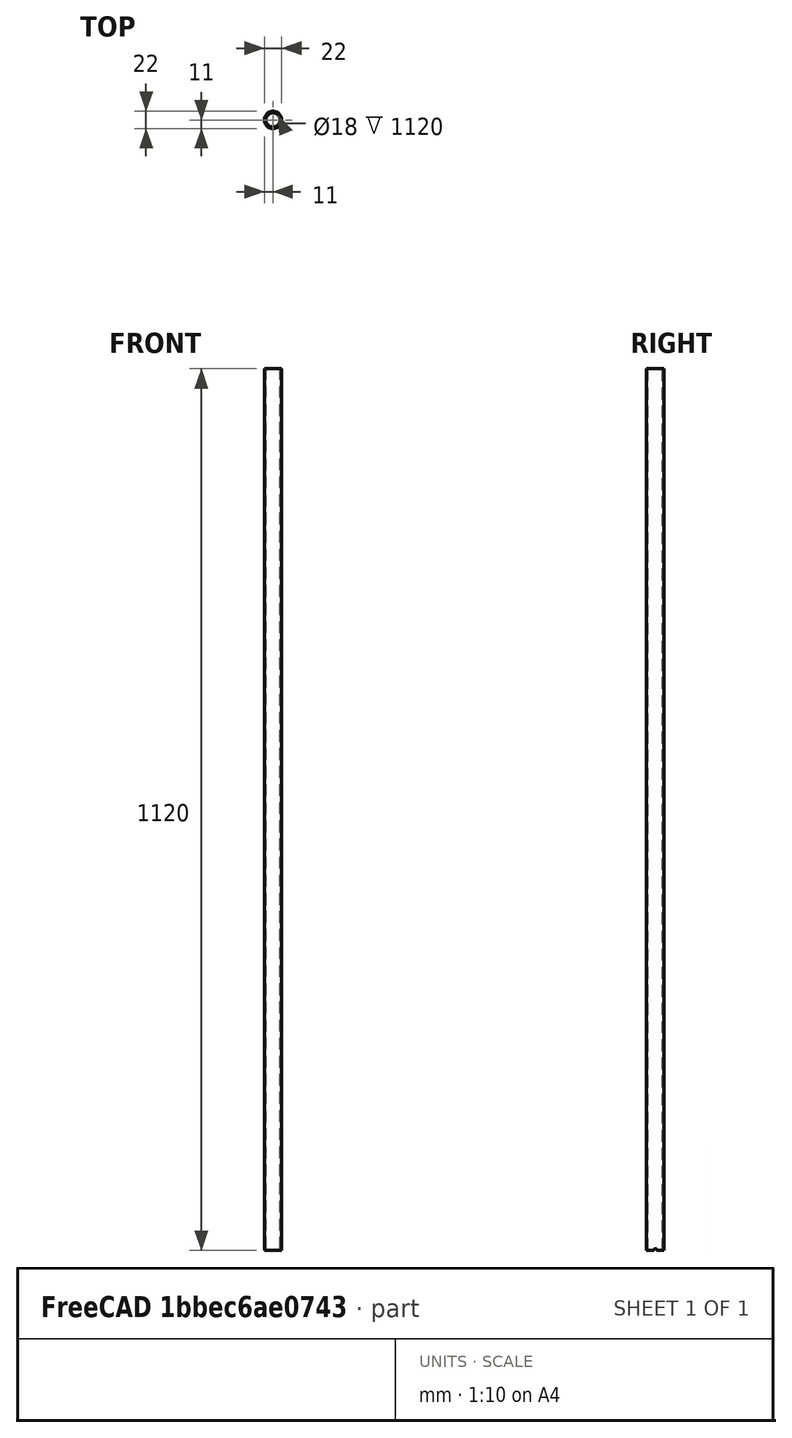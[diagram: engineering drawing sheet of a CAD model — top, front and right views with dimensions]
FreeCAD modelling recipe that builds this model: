
FCSTD DOCUMENT  (FreeCAD 0.18.3R)
Label: bar_112cm
License: All rights reserved
LicenseURL: http://en.wikipedia.org/wiki/All_rights_reserved
objects: Part::Cylinder×3, Part::Cut×2, PartDesign::FeatureBase×1, PartDesign::Body×1
note: 7 computed .brp shape members not serialized (recipe doc carries the construction recipe); baked Part::Feature solids carry a one-line shape summary decoded from their .brp

FEATURE [Part::Cylinder] Cylinder
  Angle = 360
  AttacherType = Attacher::AttachEngine3D
  Height = 1120
  Radius = 11
FEATURE [Part::Cylinder] Cylinder001
  Angle = 360
  AttacherType = Attacher::AttachEngine3D
  Height = 1120
  Radius = 9
FEATURE [Part::Cut] Cut
  Base = -> Cylinder
  Tool = -> Cylinder001
FEATURE [Part::Cylinder] Cylinder002
  Angle = 360
  AttacherType = Attacher::AttachEngine3D
  Height = 22
  Placement = pos=(-11,0,0) rot=(0,1,0;1.5708rad)
  Radius = 2
FEATURE [Part::Cut] Cut001
  Base = -> Cut
  Tool = -> Cylinder002
FEATURE [PartDesign::FeatureBase] BaseFeature
  BaseFeature = -> Cut001
FEATURE [PartDesign::Body] Body
  BaseFeature = -> Cut001
  Group = -> [BaseFeature]
  Origin = -> Origin
  Tip = -> BaseFeature
